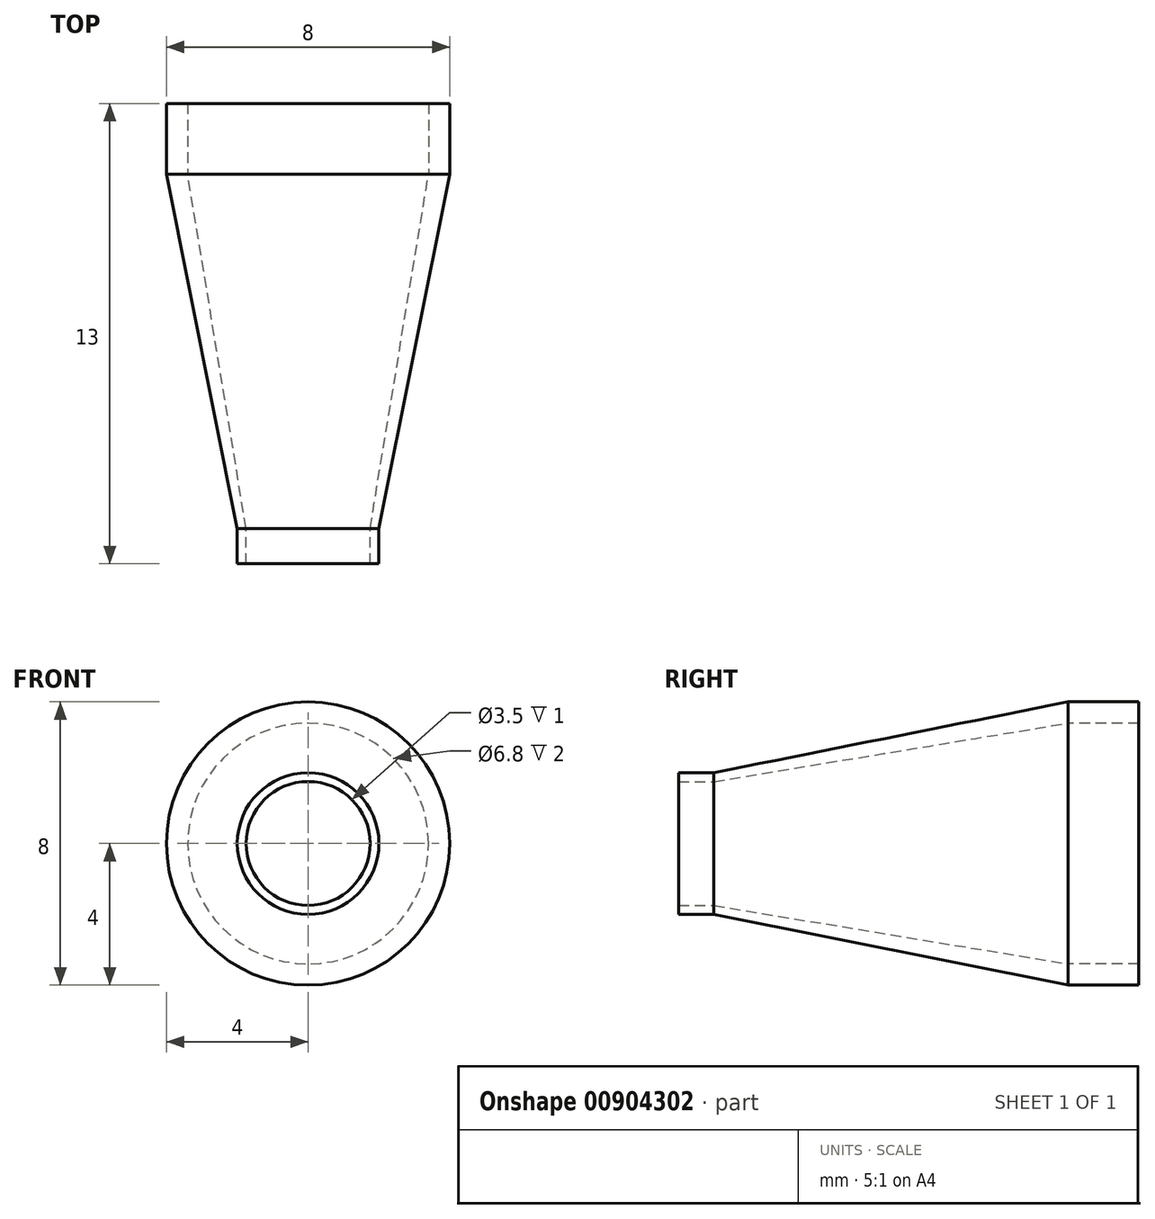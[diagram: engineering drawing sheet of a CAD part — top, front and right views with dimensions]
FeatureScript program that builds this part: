
annotation { "Feature Type Name" : "Feature", "Feature Type Description" : "" }
export const myFeature = defineFeature(function(context is Context, id is Id, definition is map)
    precondition{}
    {
        {
            var Q0;
            Q0=qCreatedBy(makeId("Front.planeOp"),FACE);
            cPlane(context, id + "F0", {"entities" : qUnion([Q0]), "cplaneType" : CPlaneType.OFFSET, "offset" : 10 * mm, "width" : 150 * mm, "height" : 150 * mm});
        }
        {
            var Q0;
            Q0=qCreatedBy(makeId("Front.planeOp"),FACE);
            var sketch = newSketch(context, id + "F1", { "sketchPlane" : qUnion([Q0])});
            skCircle(sketch, "E0", {"center": v(0, 0) * mm, "radius": 4 * mm});
            skCircle(sketch, "E1", {"center": v(0, 0) * mm, "radius": 3.4 * mm});
            skSolve(sketch);
        }
        {
            var Q0;
            Q0=qCreatedBy(id+"F0.planeOp",FACE);
            var sketch = newSketch(context, id + "F2", { "sketchPlane" : qUnion([Q0])});
            skCircle(sketch, "E2", {"center": v(0, 0) * mm, "radius": 1.75 * mm});
            skCircle(sketch, "E3", {"center": v(0, 0) * mm, "radius": 2 * mm});
            skSolve(sketch);
        }
        {
            var Q0;
            Q0=makeQuery(id+"F2.imprint","IMPRINT",FACE,{"disambiguationData":[TD([[makeQuery(id+"F2.imprint","IMPRINT",EDGE,{"derivedFrom":sQuery(id+"F2.wireOp",EDGE,"E2")}),-1.0]])]});
            extrude(context, id + "F3", {"entities" : qUnion([Q0]), "depth" : 2 * mm, "offsetDistance" : 25 * mm});
        }
        {
            var Q0;
            Q0=makeQuery(id+"F1.imprint","IMPRINT",FACE,{"disambiguationData":[TD([[makeQuery(id+"F1.imprint","IMPRINT",EDGE,{"derivedFrom":sQuery(id+"F1.wireOp",EDGE,"E0")}),1.0]])]});
            extrude(context, id + "F4", {"entities" : qUnion([Q0]), "oppositeDirection" : true, "depth" : 2 * mm, "offsetDistance" : 25 * mm});
        }
        {
            var Q0;
            Q0=qCreatedBy(makeId("Right.planeOp"),FACE);
            var sketch = newSketch(context, id + "F5", { "sketchPlane" : qUnion([Q0])});
            skLineSegment(sketch, "E4.0", {"start": v(0, -4) * mm, "end": v(0, 4) * mm});
            skLineSegment(sketch, "E5.0", {"start": v(-10, -2) * mm, "end": v(-10, 2) * mm});
            skLineSegment(sketch, "E6.0", {"start": v(-10, -1.75) * mm, "end": v(-10, 1.75) * mm});
            skLineSegment(sketch, "E7.0", {"start": v(0, -3.4) * mm, "end": v(0, 3.4) * mm});
            skLineSegment(sketch, "E8", {"start": v(0, -3.4) * mm, "end": v(-10, -1.75) * mm});
            skLineSegment(sketch, "E9", {"start": v(0, -4) * mm, "end": v(-10, -2) * mm});
            skLineSegment(sketch, "E10", {"start": v(0, 0) * mm, "end": v(-10, 0) * mm});
            skSolve(sketch);
        }
        {
            var Q0;
            {var subQ2=sQuery(id+"F5.wireOp",EDGE,"E8");Q0=makeQuery(id+"F5.imprint","IMPRINT",FACE,{"disambiguationData":[TD([[makeQuery(id+"F5.imprint","IMPRINT",EDGE,{"derivedFrom":subQ2}),1.0]])]});}
            var Q1;
            Q1=sQuery(id+"F5.wireOp",EDGE,"E10");
            revolve(context, id + "F6", {"surfaceOperationType" : NewSurfaceOperationType.NEW, "entities" : qUnion([Q0]), "axis" : qUnion([Q1]), "revolveType" : RevolveType.FULL});
        }
        {
            var Q0;
            Q0=makeQuery(id+"F3.opExtrude","CAP_FACE",FACE,{"disambiguationData":[OSD([sQuery(id+"F2.wireOp",EDGE,"E2"),sQuery(id+"F2.wireOp",EDGE,"E3")])],"isStart":false});
            extrude(context, id + "F7", {"entities" : qUnion([Q0]), "operationType" : NewBodyOperationType.REMOVE, "oppositeDirection" : true, "depth" : 1.9 * mm, "offsetDistance" : 25 * mm});
        }
        {
            var Q0;
            Q0=makeQuery(id+"F4.opExtrude","CAP_FACE",FACE,{"disambiguationData":[OSD([sQuery(id+"F1.wireOp",EDGE,"E0"),sQuery(id+"F1.wireOp",EDGE,"E1")])],"isStart":false});
            extrude(context, id + "F8", {"entities" : qUnion([Q0]), "operationType" : NewBodyOperationType.REMOVE, "oppositeDirection" : true, "depth" : 1.9 * mm, "offsetDistance" : 25 * mm});
        }
        {
            var Q0;
            Q0=makeQuery(id+"F7.boolean.opBoolean","COPY",FACE,{"derivedFrom":makeQuery(id+"F7.opExtrude","CAP_FACE",FACE,{"disambiguationData":[OSD([sQuery(id+"F2.wireOp",EDGE,"E2"),sQuery(id+"F2.wireOp",EDGE,"E3")])],"isStart":false})});
            extrude(context, id + "F9", {"entities" : qUnion([Q0]), "operationType" : NewBodyOperationType.ADD, "depth" : 0.9 * mm, "offsetDistance" : 25 * mm});
        }
        {
            var Q0;
            Q0=makeQuery(id+"F8.boolean.opBoolean","COPY",FACE,{"derivedFrom":makeQuery(id+"F8.opExtrude","CAP_FACE",FACE,{"disambiguationData":[OSD([sQuery(id+"F1.wireOp",EDGE,"E0"),sQuery(id+"F1.wireOp",EDGE,"E1")])],"isStart":false})});
            extrude(context, id + "F10", {"entities" : qUnion([Q0]), "operationType" : NewBodyOperationType.ADD, "depth" : 1.9 * mm, "offsetDistance" : 25 * mm});
        }
    });
